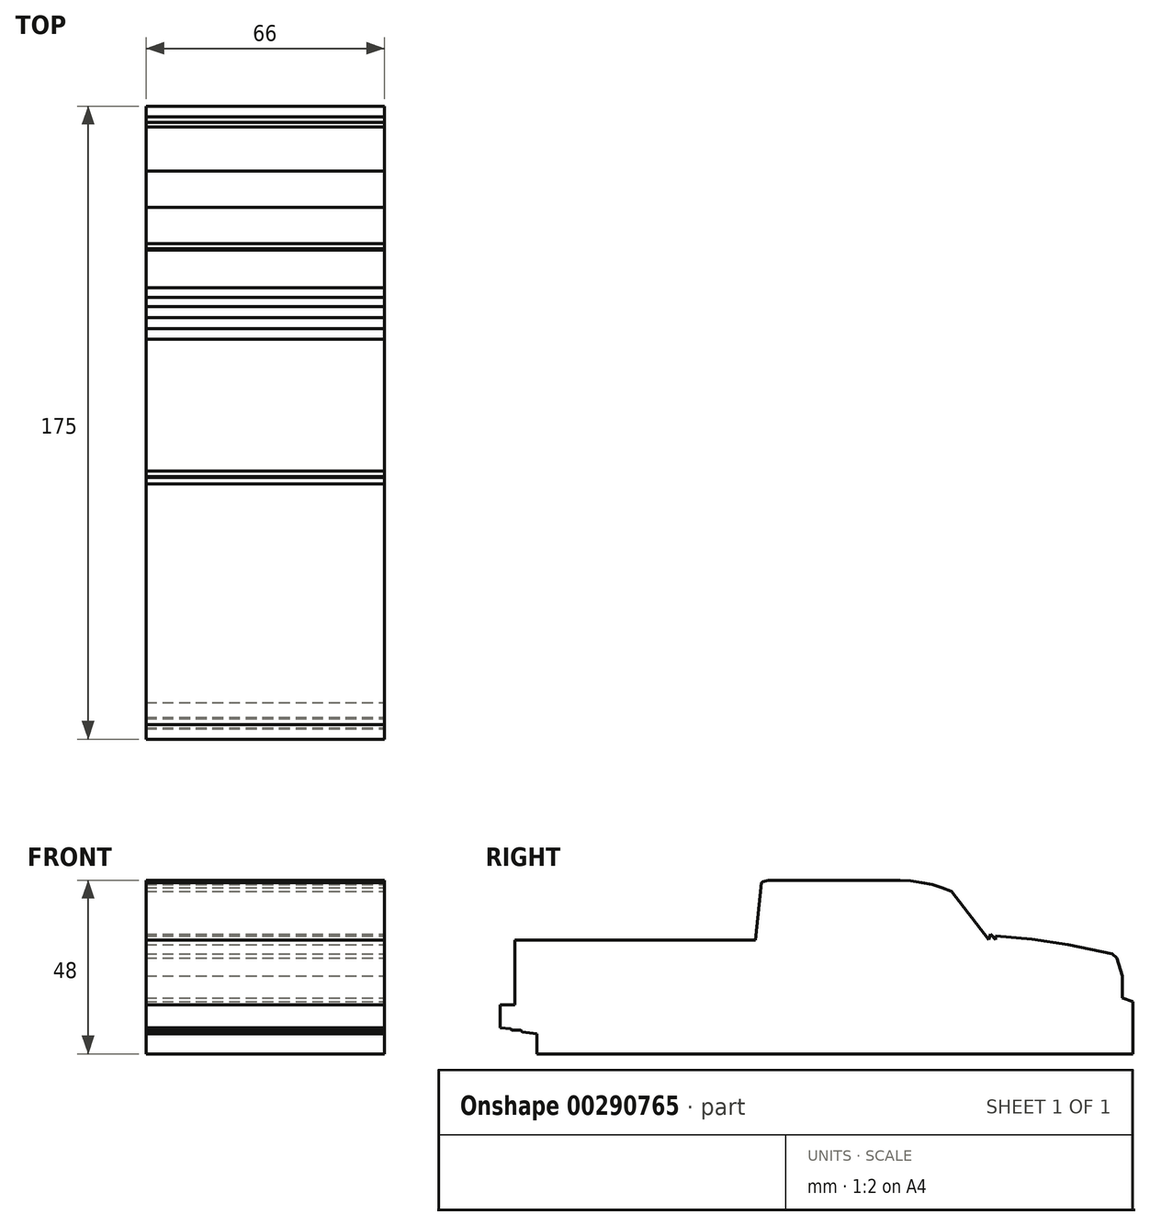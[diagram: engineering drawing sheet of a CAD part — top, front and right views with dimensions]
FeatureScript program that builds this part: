
annotation { "Feature Type Name" : "Feature", "Feature Type Description" : "" }
export const myFeature = defineFeature(function(context is Context, id is Id, definition is map)
    precondition{}
    {
        {
            var Q0;
            Q0=qCreatedBy(makeId("Right.planeOp"),FACE);
            var sketch = newSketch(context, id + "F0", { "sketchPlane" : qUnion([Q0])});
            skPoint(sketch, "E0.middle", {"position": v(0, 0) * mm});
            skLineSegment(sketch, "E1", {"start": v(-77.41, -24) * mm, "end": v(-77.41, -18.5) * mm});
            skLineSegment(sketch, "E2", {"start": v(-77.41, -18.5) * mm, "end": v(-81.41, -18) * mm});
            skLineSegment(sketch, "E3", {"start": v(-84.41, -17.5) * mm, "end": v(-81.8, -17.5) * mm});
            skLineSegment(sketch, "E4", {"start": v(-81.8, -17.5) * mm, "end": v(-81.41, -18) * mm});
            skLineSegment(sketch, "E5", {"start": v(-87.5, -16.75) * mm, "end": v(-84.63, -17.13) * mm});
            skLineSegment(sketch, "E6", {"start": v(-84.63, -17.13) * mm, "end": v(-84.41, -17.5) * mm});
            skLineSegment(sketch, "E7", {"start": v(23.03, 24) * mm, "end": v(26.03, 23.77) * mm});
            skLineSegment(sketch, "E8", {"start": v(26.03, 23.77) * mm, "end": v(29.03, 23.32) * mm});
            skLineSegment(sketch, "E9", {"start": v(29.03, 23.32) * mm, "end": v(32.02, 22.77) * mm});
            skLineSegment(sketch, "E10", {"start": v(34.68, 21.91) * mm, "end": v(32.02, 22.77) * mm});
            skLineSegment(sketch, "E11", {"start": v(34.68, 21.91) * mm, "end": v(37.33, 20.85) * mm});
            skLineSegment(sketch, "E12", {"start": v(-14.93, 23.54) * mm, "end": v(-13.39, 24) * mm});
            skLineSegment(sketch, "E13", {"start": v(-14.93, 23.54) * mm, "end": v(-15.22, 23.29) * mm});
            skLineSegment(sketch, "E14", {"start": v(-15.22, 23.29) * mm, "end": v(-16.97, 7.5) * mm});
            skLineSegment(sketch, "E15", {"start": v(47.66, 7.59) * mm, "end": v(37.33, 20.85) * mm});
            skLineSegment(sketch, "E16", {"start": v(49.52, 7.59) * mm, "end": v(49.52, 7.92) * mm});
            skLineSegment(sketch, "E17", {"start": v(84.49, -8.53) * mm, "end": v(87.5, -9.63) * mm});
            skLineSegment(sketch, "E18", {"start": v(84.49, -8.53) * mm, "end": v(84.49, -2.43) * mm});
            skLineSegment(sketch, "E19", {"start": v(84.49, -2.43) * mm, "end": v(82.97, 2.48) * mm});
            skLineSegment(sketch, "E20", {"start": v(82.97, 2.48) * mm, "end": v(81.7, 3.64) * mm});
            skLineSegment(sketch, "E21", {"start": v(81.7, 3.64) * mm, "end": v(69.56, 6.18) * mm});
            skLineSegment(sketch, "E22", {"start": v(-87.5, -10.52) * mm, "end": v(-83.49, -10.52) * mm});
            skLineSegment(sketch, "E23", {"start": v(-83.49, 7.5) * mm, "end": v(-83.49, -10.52) * mm});
            skLineSegment(sketch, "E24", {"start": v(47.66, 7.59) * mm, "end": v(48.05, 9.14) * mm});
            skLineSegment(sketch, "E25", {"start": v(48.05, 9.14) * mm, "end": v(49.52, 7.59) * mm});
            skLineSegment(sketch, "E26", {"start": v(49.52, 8.53) * mm, "end": v(49.52, 7.59) * mm});
            skLineSegment(sketch, "E27", {"start": v(69.56, 6.18) * mm, "end": v(59.54, 7.67) * mm});
            skLineSegment(sketch, "E28", {"start": v(59.54, 7.67) * mm, "end": v(49.52, 8.53) * mm});
            skLineSegment(sketch, "E29", {"start": v(-16.97, 7.5) * mm, "end": v(-83.49, 7.5) * mm});
            skLineSegment(sketch, "E30", {"start": v(-87.5, -16.75) * mm, "end": v(-87.5, -10.52) * mm});
            skLineSegment(sketch, "E31", {"start": v(87.5, -24) * mm, "end": v(-77.41, -24) * mm});
            skLineSegment(sketch, "E32", {"start": v(23.03, 24) * mm, "end": v(-13.39, 24) * mm});
            skLineSegment(sketch, "E33", {"start": v(87.5, -9.63) * mm, "end": v(87.5, -24) * mm});
            skSolve(sketch);
        }
        {
            var Q0;
            Q0 = qSketchRegion(id + "F0", true);
            var Q1;
            {var subQ5=sQuery(id+"F0.wireOp",EDGE,"E0.bottom");Q1=makeQuery(id+"F0.imprint","IMPRINT",FACE,{"disambiguationData":[TD([[makeQuery(id+"F0.imprint","IMPRINT",EDGE,{"derivedFrom":subQ5}),1.0]])]});}
            extrude(context, id + "F1", {"entities" : qUnion([Q0, Q1]), "oppositeDirection" : true, "depth" : 66 * mm});
        }
    });
